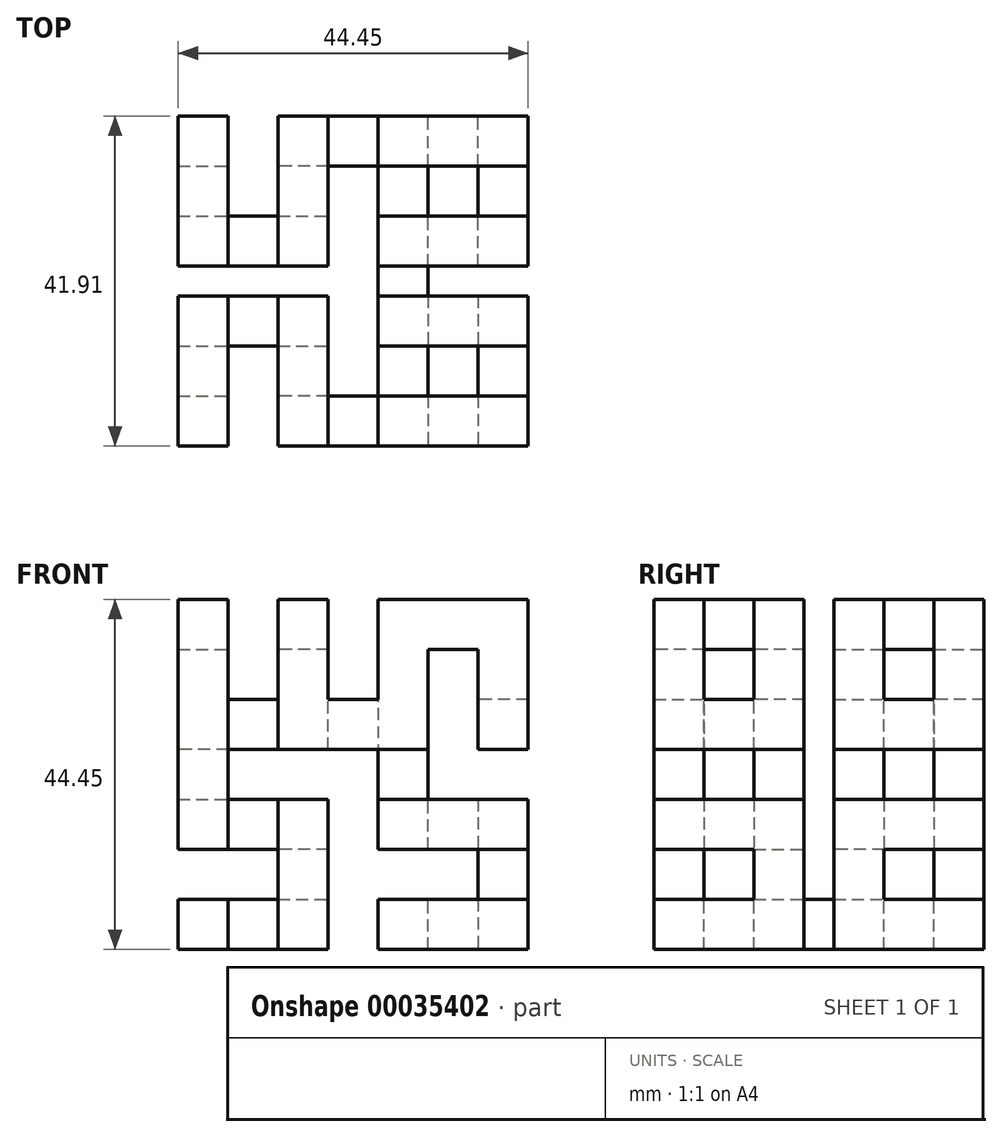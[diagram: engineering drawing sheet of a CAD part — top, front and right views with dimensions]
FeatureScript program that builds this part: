
annotation { "Feature Type Name" : "Feature", "Feature Type Description" : "" }
export const myFeature = defineFeature(function(context is Context, id is Id, definition is map)
    precondition{}
    {
        {
            var Q0;
            Q0=qCreatedBy(makeId("Front.planeOp"),FACE);
            var sketch = newSketch(context, id + "F0", { "sketchPlane" : qUnion([Q0])});
            skLineSegment(sketch, "E0.bottom", {"start": v(0, 0) * mm, "end": v(6.35, 0) * mm});
            skLineSegment(sketch, "E0.top", {"start": v(0, 6.35) * mm, "end": v(6.35, 6.35) * mm});
            skLineSegment(sketch, "E0.left", {"start": v(0, 0) * mm, "end": v(0, 6.35) * mm});
            skLineSegment(sketch, "E0.right", {"start": v(6.35, 0) * mm, "end": v(6.35, 6.35) * mm});
            skSolve(sketch);
        }
        {
            var Q0;
            Q0=makeQuery(id+"F0.imprint","IMPRINT",FACE,{"disambiguationData":[TD([[makeQuery(id+"F0.imprint","IMPRINT",EDGE,{"derivedFrom":sQuery(id+"F0.wireOp",EDGE,"E0.bottom")}),1.0]])]});
            extrude(context, id + "F1", {"entities" : qUnion([Q0]), "depth" : 19.05 * mm});
        }
        {
            var Q0;
            Q0=makeQuery(id+"F1.opExtrude","SWEPT_FACE",FACE,{"disambiguationData":[OSD([sQuery(id+"F0.wireOp",EDGE,"E0.left")])]});
            var sketch = newSketch(context, id + "F2", { "sketchPlane" : qUnion([Q0])});
            skLineSegment(sketch, "E1.bottom", {"start": v(19.05, 6.35) * mm, "end": v(12.7, 6.35) * mm});
            skLineSegment(sketch, "E1.top", {"start": v(19.05, 0) * mm, "end": v(12.7, 0) * mm});
            skLineSegment(sketch, "E1.left", {"start": v(19.05, 6.35) * mm, "end": v(19.05, 0) * mm});
            skLineSegment(sketch, "E1.right", {"start": v(12.7, 6.35) * mm, "end": v(12.7, 0) * mm});
            skSolve(sketch);
        }
        {
            var Q0;
            Q0=makeQuery(id+"F2.imprint","IMPRINT",FACE,{"disambiguationData":[TD([[makeQuery(id+"F2.imprint","IMPRINT",EDGE,{"derivedFrom":sQuery(id+"F2.wireOp",EDGE,"E1.bottom")}),1.0]])]});
            extrude(context, id + "F3", {"entities" : qUnion([Q0]), "operationType" : NewBodyOperationType.ADD, "oppositeDirection" : true, "depth" : 19.05 * mm});
        }
        {
            var Q0;
            Q0=makeQuery(id+"F3.boolean.opBoolean","MERGE",FACE,{"derivedFrom":[makeQuery(id+"F1.opExtrude","CAP_FACE",FACE,{"disambiguationData":[OSD([sQuery(id+"F0.wireOp",EDGE,"E0.bottom"),sQuery(id+"F0.wireOp",EDGE,"E0.top"),sQuery(id+"F0.wireOp",EDGE,"E0.left"),sQuery(id+"F0.wireOp",EDGE,"E0.right")])],"isStart":false}),makeQuery(id+"F3.opExtrude","SWEPT_FACE",FACE,{"disambiguationData":[OSD([sQuery(id+"F2.wireOp",EDGE,"E1.left")])]})]});
            var sketch = newSketch(context, id + "F4", { "sketchPlane" : qUnion([Q0])});
            skLineSegment(sketch, "E2.bottom", {"start": v(19.05, 6.35) * mm, "end": v(12.7, 6.35) * mm});
            skLineSegment(sketch, "E2.top", {"start": v(19.05, 0) * mm, "end": v(12.7, 0) * mm});
            skLineSegment(sketch, "E2.left", {"start": v(19.05, 6.35) * mm, "end": v(19.05, 0) * mm});
            skLineSegment(sketch, "E2.right", {"start": v(12.7, 6.35) * mm, "end": v(12.7, 0) * mm});
            skSolve(sketch);
        }
        {
            var Q0;
            Q0=makeQuery(id+"F4.imprint","IMPRINT",FACE,{"disambiguationData":[TD([[makeQuery(id+"F4.imprint","IMPRINT",EDGE,{"derivedFrom":sQuery(id+"F4.wireOp",EDGE,"E2.bottom")}),-1.0]])]});
            extrude(context, id + "F5", {"entities" : qUnion([Q0]), "operationType" : NewBodyOperationType.ADD, "oppositeDirection" : true, "depth" : 19.05 * mm});
        }
        {
            var Q0;
            Q0=makeQuery(id+"F5.boolean.opBoolean","MERGE",FACE,{"derivedFrom":[makeQuery(id+"F3.boolean.opBoolean","MERGE",FACE,{"derivedFrom":[makeQuery(id+"F1.opExtrude","SWEPT_FACE",FACE,{"disambiguationData":[OSD([sQuery(id+"F0.wireOp",EDGE,"E0.bottom")])]}),makeQuery(id+"F3.opExtrude","SWEPT_FACE",FACE,{"disambiguationData":[OSD([sQuery(id+"F2.wireOp",EDGE,"E1.top")])]})]}),makeQuery(id+"F5.opExtrude","SWEPT_FACE",FACE,{"disambiguationData":[OSD([sQuery(id+"F4.wireOp",EDGE,"E2.top")])]})]});
            var sketch = newSketch(context, id + "F6", { "sketchPlane" : qUnion([Q0])});
            skLineSegment(sketch, "E3.bottom", {"start": v(19.05, 0) * mm, "end": v(12.7, 0) * mm});
            skLineSegment(sketch, "E3.top", {"start": v(19.05, 6.35) * mm, "end": v(12.7, 6.35) * mm});
            skLineSegment(sketch, "E3.left", {"start": v(19.05, 0) * mm, "end": v(19.05, 6.35) * mm});
            skLineSegment(sketch, "E3.right", {"start": v(12.7, 0) * mm, "end": v(12.7, 6.35) * mm});
            skSolve(sketch);
        }
        {
            var Q0;
            Q0=makeQuery(id+"F6.imprint","IMPRINT",FACE,{"disambiguationData":[TD([[makeQuery(id+"F6.imprint","IMPRINT",EDGE,{"derivedFrom":sQuery(id+"F6.wireOp",EDGE,"E3.bottom")}),1.0]])]});
            extrude(context, id + "F7", {"entities" : qUnion([Q0]), "operationType" : NewBodyOperationType.ADD, "oppositeDirection" : true, "depth" : 19.05 * mm});
        }
        {
            var Q0;
            Q0=makeQuery(id+"F7.boolean.opBoolean","MERGE",FACE,{"derivedFrom":[makeQuery(id+"F5.opExtrude","CAP_FACE",FACE,{"disambiguationData":[OSD([sQuery(id+"F4.wireOp",EDGE,"E2.bottom"),sQuery(id+"F4.wireOp",EDGE,"E2.top"),sQuery(id+"F4.wireOp",EDGE,"E2.left"),sQuery(id+"F4.wireOp",EDGE,"E2.right")])],"isStart":false}),makeQuery(id+"F7.opExtrude","SWEPT_FACE",FACE,{"disambiguationData":[OSD([sQuery(id+"F6.wireOp",EDGE,"E3.bottom")])]})]});
            var sketch = newSketch(context, id + "F8", { "sketchPlane" : qUnion([Q0])});
            skLineSegment(sketch, "E4.bottom", {"start": v(-12.7, 19.05) * mm, "end": v(-19.05, 19.05) * mm});
            skLineSegment(sketch, "E4.top", {"start": v(-12.7, 12.7) * mm, "end": v(-19.05, 12.7) * mm});
            skLineSegment(sketch, "E4.left", {"start": v(-12.7, 19.05) * mm, "end": v(-12.7, 12.7) * mm});
            skLineSegment(sketch, "E4.right", {"start": v(-19.05, 19.05) * mm, "end": v(-19.05, 12.7) * mm});
            skSolve(sketch);
        }
        {
            var Q0;
            Q0=makeQuery(id+"F8.imprint","IMPRINT",FACE,{"disambiguationData":[TD([[makeQuery(id+"F8.imprint","IMPRINT",EDGE,{"derivedFrom":sQuery(id+"F8.wireOp",EDGE,"E4.bottom")}),1.0]])]});
            extrude(context, id + "F9", {"entities" : qUnion([Q0]), "operationType" : NewBodyOperationType.ADD, "oppositeDirection" : true, "depth" : 19.05 * mm});
        }
        {
            var Q0;
            Q0=makeQuery(id+"F9.boolean.opBoolean","MERGE",FACE,{"derivedFrom":[makeQuery(id+"F7.boolean.opBoolean","MERGE",FACE,{"derivedFrom":[makeQuery(id+"F5.boolean.opBoolean","MERGE",FACE,{"derivedFrom":[makeQuery(id+"F3.opExtrude","CAP_FACE",FACE,{"disambiguationData":[OSD([sQuery(id+"F2.wireOp",EDGE,"E1.bottom"),sQuery(id+"F2.wireOp",EDGE,"E1.top"),sQuery(id+"F2.wireOp",EDGE,"E1.left"),sQuery(id+"F2.wireOp",EDGE,"E1.right")])],"isStart":false}),makeQuery(id+"F5.opExtrude","SWEPT_FACE",FACE,{"disambiguationData":[OSD([sQuery(id+"F4.wireOp",EDGE,"E2.left")])]})]}),makeQuery(id+"F7.opExtrude","SWEPT_FACE",FACE,{"disambiguationData":[OSD([sQuery(id+"F6.wireOp",EDGE,"E3.left")])]})]}),makeQuery(id+"F9.opExtrude","SWEPT_FACE",FACE,{"disambiguationData":[OSD([sQuery(id+"F8.wireOp",EDGE,"E4.right")])]})]});
            var sketch = newSketch(context, id + "F10", { "sketchPlane" : qUnion([Q0])});
            skLineSegment(sketch, "E5.bottom", {"start": v(-19.05, 19.05) * mm, "end": v(-12.7, 19.05) * mm});
            skLineSegment(sketch, "E5.top", {"start": v(-19.05, 12.7) * mm, "end": v(-12.7, 12.7) * mm});
            skLineSegment(sketch, "E5.left", {"start": v(-19.05, 19.05) * mm, "end": v(-19.05, 12.7) * mm});
            skLineSegment(sketch, "E5.right", {"start": v(-12.7, 19.05) * mm, "end": v(-12.7, 12.7) * mm});
            skSolve(sketch);
        }
        {
            var Q0;
            Q0=makeQuery(id+"F10.imprint","IMPRINT",FACE,{"disambiguationData":[TD([[makeQuery(id+"F10.imprint","IMPRINT",EDGE,{"derivedFrom":sQuery(id+"F10.wireOp",EDGE,"E5.bottom")}),-1.0]])]});
            extrude(context, id + "F11", {"entities" : qUnion([Q0]), "operationType" : NewBodyOperationType.ADD, "oppositeDirection" : true, "depth" : 19.05 * mm});
        }
        {
            var Q0;
            Q0=makeQuery(id+"F11.boolean.opBoolean","MERGE",FACE,{"derivedFrom":[makeQuery(id+"F9.opExtrude","CAP_FACE",FACE,{"disambiguationData":[OSD([sQuery(id+"F8.wireOp",EDGE,"E4.bottom"),sQuery(id+"F8.wireOp",EDGE,"E4.top"),sQuery(id+"F8.wireOp",EDGE,"E4.left"),sQuery(id+"F8.wireOp",EDGE,"E4.right")])],"isStart":false}),makeQuery(id+"F11.opExtrude","SWEPT_FACE",FACE,{"disambiguationData":[OSD([sQuery(id+"F10.wireOp",EDGE,"E5.left")])]})]});
            var sketch = newSketch(context, id + "F12", { "sketchPlane" : qUnion([Q0])});
            skLineSegment(sketch, "E6.bottom", {"start": v(0, 19.05) * mm, "end": v(6.35, 19.05) * mm});
            skLineSegment(sketch, "E6.top", {"start": v(0, 12.7) * mm, "end": v(6.35, 12.7) * mm});
            skLineSegment(sketch, "E6.left", {"start": v(0, 19.05) * mm, "end": v(0, 12.7) * mm});
            skLineSegment(sketch, "E6.right", {"start": v(6.35, 19.05) * mm, "end": v(6.35, 12.7) * mm});
            skSolve(sketch);
        }
        {
            var Q0;
            Q0=makeQuery(id+"F12.imprint","IMPRINT",FACE,{"disambiguationData":[TD([[makeQuery(id+"F12.imprint","IMPRINT",EDGE,{"derivedFrom":sQuery(id+"F12.wireOp",EDGE,"E6.bottom")}),-1.0]])]});
            extrude(context, id + "F13", {"entities" : qUnion([Q0]), "operationType" : NewBodyOperationType.ADD, "oppositeDirection" : true, "depth" : 19.05 * mm});
        }
        {
            var Q0;
            Q0=makeQuery(id+"F13.boolean.opBoolean","MERGE",FACE,{"derivedFrom":[makeQuery(id+"F11.boolean.opBoolean","MERGE",FACE,{"derivedFrom":[makeQuery(id+"F9.opExtrude","SWEPT_FACE",FACE,{"disambiguationData":[OSD([sQuery(id+"F8.wireOp",EDGE,"E4.top")])]}),makeQuery(id+"F11.opExtrude","SWEPT_FACE",FACE,{"disambiguationData":[OSD([sQuery(id+"F10.wireOp",EDGE,"E5.top")])]})]}),makeQuery(id+"F13.opExtrude","SWEPT_FACE",FACE,{"disambiguationData":[OSD([sQuery(id+"F12.wireOp",EDGE,"E6.top")])]})]});
            var sketch = newSketch(context, id + "F14", { "sketchPlane" : qUnion([Q0])});
            skLineSegment(sketch, "E7.bottom", {"start": v(0, 0) * mm, "end": v(6.35, 0) * mm});
            skLineSegment(sketch, "E7.top", {"start": v(0, 6.35) * mm, "end": v(6.35, 6.35) * mm});
            skLineSegment(sketch, "E7.left", {"start": v(0, 0) * mm, "end": v(0, 6.35) * mm});
            skLineSegment(sketch, "E7.right", {"start": v(6.35, 0) * mm, "end": v(6.35, 6.35) * mm});
            skSolve(sketch);
        }
        {
            var Q0;
            Q0=makeQuery(id+"F14.imprint","IMPRINT",FACE,{"disambiguationData":[TD([[makeQuery(id+"F14.imprint","IMPRINT",EDGE,{"derivedFrom":sQuery(id+"F14.wireOp",EDGE,"E7.bottom")}),1.0]])]});
            extrude(context, id + "F15", {"entities" : qUnion([Q0]), "operationType" : NewBodyOperationType.ADD, "oppositeDirection" : true, "depth" : 31.75 * mm});
        }
        {
            var Q0;
            Q0=makeQuery(id+"F15.boolean.opBoolean","MERGE",FACE,{"derivedFrom":[makeQuery(id+"F13.opExtrude","CAP_FACE",FACE,{"disambiguationData":[OSD([sQuery(id+"F12.wireOp",EDGE,"E6.bottom"),sQuery(id+"F12.wireOp",EDGE,"E6.top"),sQuery(id+"F12.wireOp",EDGE,"E6.left"),sQuery(id+"F12.wireOp",EDGE,"E6.right")])],"isStart":false}),makeQuery(id+"F15.opExtrude","SWEPT_FACE",FACE,{"disambiguationData":[OSD([sQuery(id+"F14.wireOp",EDGE,"E7.bottom")])]})]});
            var sketch = newSketch(context, id + "F16", { "sketchPlane" : qUnion([Q0])});
            skLineSegment(sketch, "E8.bottom", {"start": v(-6.35, 44.45) * mm, "end": v(0, 44.45) * mm});
            skLineSegment(sketch, "E8.top", {"start": v(-6.35, 38.1) * mm, "end": v(0, 38.1) * mm});
            skLineSegment(sketch, "E8.left", {"start": v(-6.35, 44.45) * mm, "end": v(-6.35, 38.1) * mm});
            skLineSegment(sketch, "E8.right", {"start": v(0, 44.45) * mm, "end": v(0, 38.1) * mm});
            skSolve(sketch);
        }
        {
            var Q0;
            Q0=makeQuery(id+"F16.imprint","IMPRINT",FACE,{"disambiguationData":[TD([[makeQuery(id+"F16.imprint","IMPRINT",EDGE,{"derivedFrom":sQuery(id+"F16.wireOp",EDGE,"E8.bottom")}),1.0]])]});
            extrude(context, id + "F17", {"entities" : qUnion([Q0]), "operationType" : NewBodyOperationType.ADD, "oppositeDirection" : true, "depth" : 19.05 * mm});
        }
        {
            var Q0;
            Q0=makeQuery(id+"F17.boolean.opBoolean","MERGE",FACE,{"derivedFrom":[makeQuery(id+"F15.opExtrude","CAP_FACE",FACE,{"disambiguationData":[OSD([sQuery(id+"F14.wireOp",EDGE,"E7.bottom"),sQuery(id+"F14.wireOp",EDGE,"E7.top"),sQuery(id+"F14.wireOp",EDGE,"E7.left"),sQuery(id+"F14.wireOp",EDGE,"E7.right")])],"isStart":false}),makeQuery(id+"F17.opExtrude","SWEPT_FACE",FACE,{"disambiguationData":[OSD([sQuery(id+"F16.wireOp",EDGE,"E8.bottom")])]})]});
            var sketch = newSketch(context, id + "F18", { "sketchPlane" : qUnion([Q0])});
            skLineSegment(sketch, "E9.bottom", {"start": v(6.35, -19.05) * mm, "end": v(0, -19.05) * mm});
            skLineSegment(sketch, "E9.top", {"start": v(6.35, -12.7) * mm, "end": v(0, -12.7) * mm});
            skLineSegment(sketch, "E9.left", {"start": v(6.35, -19.05) * mm, "end": v(6.35, -12.7) * mm});
            skLineSegment(sketch, "E9.right", {"start": v(0, -19.05) * mm, "end": v(0, -12.7) * mm});
            skSolve(sketch);
        }
        {
            var Q0;
            Q0=makeQuery(id+"F18.imprint","IMPRINT",FACE,{"disambiguationData":[TD([[makeQuery(id+"F18.imprint","IMPRINT",EDGE,{"derivedFrom":sQuery(id+"F18.wireOp",EDGE,"E9.bottom")}),1.0]])]});
            extrude(context, id + "F19", {"entities" : qUnion([Q0]), "operationType" : NewBodyOperationType.ADD, "oppositeDirection" : true, "depth" : 19.05 * mm});
        }
        {
            var Q0;
            Q0=makeQuery(id+"F19.boolean.opBoolean","MERGE",FACE,{"derivedFrom":[makeQuery(id+"F17.boolean.opBoolean","MERGE",FACE,{"derivedFrom":[makeQuery(id+"F15.boolean.opBoolean","MERGE",FACE,{"derivedFrom":[makeQuery(id+"F13.boolean.opBoolean","MERGE",FACE,{"derivedFrom":[makeQuery(id+"F11.opExtrude","CAP_FACE",FACE,{"disambiguationData":[OSD([sQuery(id+"F10.wireOp",EDGE,"E5.bottom"),sQuery(id+"F10.wireOp",EDGE,"E5.top"),sQuery(id+"F10.wireOp",EDGE,"E5.left"),sQuery(id+"F10.wireOp",EDGE,"E5.right")])],"isStart":false}),makeQuery(id+"F13.opExtrude","SWEPT_FACE",FACE,{"disambiguationData":[OSD([sQuery(id+"F12.wireOp",EDGE,"E6.left")])]})]}),makeQuery(id+"F15.opExtrude","SWEPT_FACE",FACE,{"disambiguationData":[OSD([sQuery(id+"F14.wireOp",EDGE,"E7.left")])]})]}),makeQuery(id+"F17.opExtrude","SWEPT_FACE",FACE,{"disambiguationData":[OSD([sQuery(id+"F16.wireOp",EDGE,"E8.right")])]})]}),makeQuery(id+"F19.opExtrude","SWEPT_FACE",FACE,{"disambiguationData":[OSD([sQuery(id+"F18.wireOp",EDGE,"E9.right")])]})]});
            var sketch = newSketch(context, id + "F20", { "sketchPlane" : qUnion([Q0])});
            skLineSegment(sketch, "E10.bottom", {"start": v(19.05, 25.4) * mm, "end": v(12.7, 25.4) * mm});
            skLineSegment(sketch, "E10.top", {"start": v(19.05, 31.75) * mm, "end": v(12.7, 31.75) * mm});
            skLineSegment(sketch, "E10.left", {"start": v(19.05, 25.4) * mm, "end": v(19.05, 31.75) * mm});
            skLineSegment(sketch, "E10.right", {"start": v(12.7, 25.4) * mm, "end": v(12.7, 31.75) * mm});
            skSolve(sketch);
        }
        {
            var Q0;
            Q0=makeQuery(id+"F20.imprint","IMPRINT",FACE,{"disambiguationData":[TD([[makeQuery(id+"F20.imprint","IMPRINT",EDGE,{"derivedFrom":sQuery(id+"F20.wireOp",EDGE,"E10.bottom")}),-1.0]])]});
            extrude(context, id + "F21", {"entities" : qUnion([Q0]), "operationType" : NewBodyOperationType.ADD, "oppositeDirection" : true, "depth" : 19.05 * mm});
        }
        {
            var Q0;
            Q0=makeQuery(id+"F21.boolean.opBoolean","MERGE",FACE,{"derivedFrom":[makeQuery(id+"F19.opExtrude","CAP_FACE",FACE,{"disambiguationData":[OSD([sQuery(id+"F18.wireOp",EDGE,"E9.bottom"),sQuery(id+"F18.wireOp",EDGE,"E9.top"),sQuery(id+"F18.wireOp",EDGE,"E9.left"),sQuery(id+"F18.wireOp",EDGE,"E9.right")])],"isStart":false}),makeQuery(id+"F21.opExtrude","SWEPT_FACE",FACE,{"disambiguationData":[OSD([sQuery(id+"F20.wireOp",EDGE,"E10.bottom")])]})]});
            var sketch = newSketch(context, id + "F22", { "sketchPlane" : qUnion([Q0])});
            skLineSegment(sketch, "E11.bottom", {"start": v(19.05, 19.05) * mm, "end": v(12.7, 19.05) * mm});
            skLineSegment(sketch, "E11.top", {"start": v(19.05, 12.7) * mm, "end": v(12.7, 12.7) * mm});
            skLineSegment(sketch, "E11.left", {"start": v(19.05, 19.05) * mm, "end": v(19.05, 12.7) * mm});
            skLineSegment(sketch, "E11.right", {"start": v(12.7, 19.05) * mm, "end": v(12.7, 12.7) * mm});
            skSolve(sketch);
        }
        {
            var Q0;
            Q0=makeQuery(id+"F22.imprint","IMPRINT",FACE,{"disambiguationData":[TD([[makeQuery(id+"F22.imprint","IMPRINT",EDGE,{"derivedFrom":sQuery(id+"F22.wireOp",EDGE,"E11.bottom")}),-1.0]])]});
            extrude(context, id + "F23", {"entities" : qUnion([Q0]), "operationType" : NewBodyOperationType.ADD, "oppositeDirection" : true, "depth" : 19.05 * mm});
        }
        {
            var Q0;
            Q0=makeQuery(id+"F23.boolean.opBoolean","MERGE",FACE,{"derivedFrom":[makeQuery(id+"F21.boolean.opBoolean","MERGE",FACE,{"derivedFrom":[makeQuery(id+"F19.boolean.opBoolean","MERGE",FACE,{"derivedFrom":[makeQuery(id+"F17.opExtrude","CAP_FACE",FACE,{"disambiguationData":[OSD([sQuery(id+"F16.wireOp",EDGE,"E8.bottom"),sQuery(id+"F16.wireOp",EDGE,"E8.top"),sQuery(id+"F16.wireOp",EDGE,"E8.left"),sQuery(id+"F16.wireOp",EDGE,"E8.right")])],"isStart":false}),makeQuery(id+"F19.opExtrude","SWEPT_FACE",FACE,{"disambiguationData":[OSD([sQuery(id+"F18.wireOp",EDGE,"E9.bottom")])]})]}),makeQuery(id+"F21.opExtrude","SWEPT_FACE",FACE,{"disambiguationData":[OSD([sQuery(id+"F20.wireOp",EDGE,"E10.left")])]})]}),makeQuery(id+"F23.opExtrude","SWEPT_FACE",FACE,{"disambiguationData":[OSD([sQuery(id+"F22.wireOp",EDGE,"E11.bottom")])]})]});
            var sketch = newSketch(context, id + "F24", { "sketchPlane" : qUnion([Q0])});
            skLineSegment(sketch, "E12.bottom", {"start": v(19.05, 44.45) * mm, "end": v(12.7, 44.45) * mm});
            skLineSegment(sketch, "E12.top", {"start": v(19.05, 38.1) * mm, "end": v(12.7, 38.1) * mm});
            skLineSegment(sketch, "E12.left", {"start": v(19.05, 44.45) * mm, "end": v(19.05, 38.1) * mm});
            skLineSegment(sketch, "E12.right", {"start": v(12.7, 44.45) * mm, "end": v(12.7, 38.1) * mm});
            skSolve(sketch);
        }
        {
            var Q0;
            Q0=makeQuery(id+"F24.imprint","IMPRINT",FACE,{"disambiguationData":[TD([[makeQuery(id+"F24.imprint","IMPRINT",EDGE,{"derivedFrom":sQuery(id+"F24.wireOp",EDGE,"E12.bottom")}),-1.0]])]});
            extrude(context, id + "F25", {"entities" : qUnion([Q0]), "operationType" : NewBodyOperationType.ADD, "oppositeDirection" : true, "depth" : 19.05 * mm});
        }
        {
            var Q0;
            Q0=makeQuery(id+"F25.boolean.opBoolean","MERGE",FACE,{"derivedFrom":[makeQuery(id+"F23.opExtrude","CAP_FACE",FACE,{"disambiguationData":[OSD([sQuery(id+"F22.wireOp",EDGE,"E11.bottom"),sQuery(id+"F22.wireOp",EDGE,"E11.top"),sQuery(id+"F22.wireOp",EDGE,"E11.left"),sQuery(id+"F22.wireOp",EDGE,"E11.right")])],"isStart":false}),makeQuery(id+"F25.opExtrude","SWEPT_FACE",FACE,{"disambiguationData":[OSD([sQuery(id+"F24.wireOp",EDGE,"E12.bottom")])]})]});
            var sketch = newSketch(context, id + "F26", { "sketchPlane" : qUnion([Q0])});
            skLineSegment(sketch, "E13.bottom", {"start": v(19.05, 0) * mm, "end": v(12.7, 0) * mm});
            skLineSegment(sketch, "E13.top", {"start": v(19.05, -6.35) * mm, "end": v(12.7, -6.35) * mm});
            skLineSegment(sketch, "E13.left", {"start": v(19.05, 0) * mm, "end": v(19.05, -6.35) * mm});
            skLineSegment(sketch, "E13.right", {"start": v(12.7, 0) * mm, "end": v(12.7, -6.35) * mm});
            skSolve(sketch);
        }
        {
            var Q0;
            Q0=makeQuery(id+"F26.imprint","IMPRINT",FACE,{"disambiguationData":[TD([[makeQuery(id+"F26.imprint","IMPRINT",EDGE,{"derivedFrom":sQuery(id+"F26.wireOp",EDGE,"E13.bottom")}),-1.0]])]});
            extrude(context, id + "F27", {"entities" : qUnion([Q0]), "operationType" : NewBodyOperationType.ADD, "oppositeDirection" : true, "depth" : 19.05 * mm});
        }
        {
            var Q0;
            Q0=makeQuery(id+"F27.boolean.opBoolean","MERGE",FACE,{"derivedFrom":[makeQuery(id+"F25.boolean.opBoolean","MERGE",FACE,{"derivedFrom":[makeQuery(id+"F23.opExtrude","SWEPT_FACE",FACE,{"disambiguationData":[OSD([sQuery(id+"F22.wireOp",EDGE,"E11.right")])]}),makeQuery(id+"F25.opExtrude","SWEPT_FACE",FACE,{"disambiguationData":[OSD([sQuery(id+"F24.wireOp",EDGE,"E12.right")])]})]}),makeQuery(id+"F27.opExtrude","SWEPT_FACE",FACE,{"disambiguationData":[OSD([sQuery(id+"F26.wireOp",EDGE,"E13.right")])]})]});
            var sketch = newSketch(context, id + "F28", { "sketchPlane" : qUnion([Q0])});
            skLineSegment(sketch, "E14.bottom", {"start": v(0, 25.4) * mm, "end": v(6.35, 25.4) * mm});
            skLineSegment(sketch, "E14.top", {"start": v(0, 31.75) * mm, "end": v(6.35, 31.75) * mm});
            skLineSegment(sketch, "E14.left", {"start": v(0, 25.4) * mm, "end": v(0, 31.75) * mm});
            skLineSegment(sketch, "E14.right", {"start": v(6.35, 25.4) * mm, "end": v(6.35, 31.75) * mm});
            skSolve(sketch);
        }
        {
            var Q0;
            Q0=makeQuery(id+"F28.imprint","IMPRINT",FACE,{"disambiguationData":[TD([[makeQuery(id+"F28.imprint","IMPRINT",EDGE,{"derivedFrom":sQuery(id+"F28.wireOp",EDGE,"E14.bottom")}),-1.0]])]});
            extrude(context, id + "F29", {"entities" : qUnion([Q0]), "operationType" : NewBodyOperationType.ADD, "oppositeDirection" : true, "depth" : 19.05 * mm});
        }
        {
            var Q0;
            Q0=makeQuery(id+"F29.boolean.opBoolean","MERGE",FACE,{"derivedFrom":[makeQuery(id+"F27.opExtrude","CAP_FACE",FACE,{"disambiguationData":[OSD([sQuery(id+"F26.wireOp",EDGE,"E13.bottom"),sQuery(id+"F26.wireOp",EDGE,"E13.top"),sQuery(id+"F26.wireOp",EDGE,"E13.left"),sQuery(id+"F26.wireOp",EDGE,"E13.right")])],"isStart":false}),makeQuery(id+"F29.opExtrude","SWEPT_FACE",FACE,{"disambiguationData":[OSD([sQuery(id+"F28.wireOp",EDGE,"E14.bottom")])]})]});
            var sketch = newSketch(context, id + "F30", { "sketchPlane" : qUnion([Q0])});
            skLineSegment(sketch, "E15.bottom", {"start": v(31.75, 0) * mm, "end": v(25.4, 0) * mm});
            skLineSegment(sketch, "E15.top", {"start": v(31.75, 6.35) * mm, "end": v(25.4, 6.35) * mm});
            skLineSegment(sketch, "E15.left", {"start": v(31.75, 0) * mm, "end": v(31.75, 6.35) * mm});
            skLineSegment(sketch, "E15.right", {"start": v(25.4, 0) * mm, "end": v(25.4, 6.35) * mm});
            skSolve(sketch);
        }
        {
            var Q0;
            Q0=makeQuery(id+"F30.imprint","IMPRINT",FACE,{"disambiguationData":[TD([[makeQuery(id+"F30.imprint","IMPRINT",EDGE,{"derivedFrom":sQuery(id+"F30.wireOp",EDGE,"E15.bottom")}),1.0]])]});
            extrude(context, id + "F31", {"entities" : qUnion([Q0]), "operationType" : NewBodyOperationType.ADD, "oppositeDirection" : true, "depth" : 19.05 * mm});
        }
        {
            var Q0;
            Q0=makeQuery(id+"F31.opExtrude","SWEPT_FACE",FACE,{"disambiguationData":[OSD([sQuery(id+"F30.wireOp",EDGE,"E15.right")])]});
            var sketch = newSketch(context, id + "F32", { "sketchPlane" : qUnion([Q0])});
            skLineSegment(sketch, "E16.bottom", {"start": v(6.35, 44.45) * mm, "end": v(0, 44.45) * mm});
            skLineSegment(sketch, "E16.top", {"start": v(6.35, 38.1) * mm, "end": v(0, 38.1) * mm});
            skLineSegment(sketch, "E16.left", {"start": v(6.35, 44.45) * mm, "end": v(6.35, 38.1) * mm});
            skLineSegment(sketch, "E16.right", {"start": v(0, 44.45) * mm, "end": v(0, 38.1) * mm});
            skSolve(sketch);
        }
        {
            var Q0;
            Q0=makeQuery(id+"F32.imprint","IMPRINT",FACE,{"disambiguationData":[TD([[makeQuery(id+"F32.imprint","IMPRINT",EDGE,{"derivedFrom":sQuery(id+"F32.wireOp",EDGE,"E16.bottom")}),-1.0]])]});
            extrude(context, id + "F33", {"entities" : qUnion([Q0]), "operationType" : NewBodyOperationType.ADD, "oppositeDirection" : true, "depth" : 19.05 * mm});
        }
        {
            var Q0;
            Q0=makeQuery(id+"F33.boolean.opBoolean","MERGE",FACE,{"derivedFrom":[makeQuery(id+"F31.opExtrude","CAP_FACE",FACE,{"disambiguationData":[OSD([sQuery(id+"F30.wireOp",EDGE,"E15.bottom"),sQuery(id+"F30.wireOp",EDGE,"E15.top"),sQuery(id+"F30.wireOp",EDGE,"E15.left"),sQuery(id+"F30.wireOp",EDGE,"E15.right")])],"isStart":false}),makeQuery(id+"F33.opExtrude","SWEPT_FACE",FACE,{"disambiguationData":[OSD([sQuery(id+"F32.wireOp",EDGE,"E16.bottom")])]})]});
            var sketch = newSketch(context, id + "F34", { "sketchPlane" : qUnion([Q0])});
            skLineSegment(sketch, "E17.bottom", {"start": v(44.45, -6.35) * mm, "end": v(38.1, -6.35) * mm});
            skLineSegment(sketch, "E17.top", {"start": v(44.45, 0) * mm, "end": v(38.1, 0) * mm});
            skLineSegment(sketch, "E17.left", {"start": v(44.45, -6.35) * mm, "end": v(44.45, 0) * mm});
            skLineSegment(sketch, "E17.right", {"start": v(38.1, -6.35) * mm, "end": v(38.1, 0) * mm});
            skSolve(sketch);
        }
        {
            var Q0;
            Q0=makeQuery(id+"F34.imprint","IMPRINT",FACE,{"disambiguationData":[TD([[makeQuery(id+"F34.imprint","IMPRINT",EDGE,{"derivedFrom":sQuery(id+"F34.wireOp",EDGE,"E17.bottom")}),-1.0]])]});
            extrude(context, id + "F35", {"entities" : qUnion([Q0]), "operationType" : NewBodyOperationType.ADD, "oppositeDirection" : true, "depth" : 19.05 * mm});
        }
        {
            var Q0;
            Q0=makeQuery(id+"F35.boolean.opBoolean","MERGE",FACE,{"derivedFrom":[makeQuery(id+"F33.boolean.opBoolean","MERGE",FACE,{"derivedFrom":[makeQuery(id+"F31.boolean.opBoolean","MERGE",FACE,{"derivedFrom":[makeQuery(id+"F29.boolean.opBoolean","MERGE",FACE,{"derivedFrom":[makeQuery(id+"F27.boolean.opBoolean","MERGE",FACE,{"derivedFrom":[makeQuery(id+"F25.opExtrude","CAP_FACE",FACE,{"disambiguationData":[OSD([sQuery(id+"F24.wireOp",EDGE,"E12.bottom"),sQuery(id+"F24.wireOp",EDGE,"E12.top"),sQuery(id+"F24.wireOp",EDGE,"E12.left"),sQuery(id+"F24.wireOp",EDGE,"E12.right")])],"isStart":false}),makeQuery(id+"F27.opExtrude","SWEPT_FACE",FACE,{"disambiguationData":[OSD([sQuery(id+"F26.wireOp",EDGE,"E13.bottom")])]})]}),makeQuery(id+"F29.opExtrude","SWEPT_FACE",FACE,{"disambiguationData":[OSD([sQuery(id+"F28.wireOp",EDGE,"E14.left")])]})]}),makeQuery(id+"F31.opExtrude","SWEPT_FACE",FACE,{"disambiguationData":[OSD([sQuery(id+"F30.wireOp",EDGE,"E15.bottom")])]})]}),makeQuery(id+"F33.opExtrude","SWEPT_FACE",FACE,{"disambiguationData":[OSD([sQuery(id+"F32.wireOp",EDGE,"E16.right")])]})]}),makeQuery(id+"F35.opExtrude","SWEPT_FACE",FACE,{"disambiguationData":[OSD([sQuery(id+"F34.wireOp",EDGE,"E17.top")])]})]});
            var sketch = newSketch(context, id + "F36", { "sketchPlane" : qUnion([Q0])});
            skLineSegment(sketch, "E18.bottom", {"start": v(-44.45, 25.4) * mm, "end": v(-38.1, 25.4) * mm});
            skLineSegment(sketch, "E18.top", {"start": v(-44.45, 31.75) * mm, "end": v(-38.1, 31.75) * mm});
            skLineSegment(sketch, "E18.left", {"start": v(-44.45, 25.4) * mm, "end": v(-44.45, 31.75) * mm});
            skLineSegment(sketch, "E18.right", {"start": v(-38.1, 25.4) * mm, "end": v(-38.1, 31.75) * mm});
            skSolve(sketch);
        }
        {
            var Q0;
            Q0=makeQuery(id+"F36.imprint","IMPRINT",FACE,{"disambiguationData":[TD([[makeQuery(id+"F36.imprint","IMPRINT",EDGE,{"derivedFrom":sQuery(id+"F36.wireOp",EDGE,"E18.bottom")}),-1.0]])]});
            extrude(context, id + "F37", {"entities" : qUnion([Q0]), "operationType" : NewBodyOperationType.ADD, "oppositeDirection" : true, "depth" : 19.05 * mm});
        }
        {
            var Q0;
            Q0=makeQuery(id+"F37.boolean.opBoolean","MERGE",FACE,{"derivedFrom":[makeQuery(id+"F35.opExtrude","CAP_FACE",FACE,{"disambiguationData":[OSD([sQuery(id+"F34.wireOp",EDGE,"E17.bottom"),sQuery(id+"F34.wireOp",EDGE,"E17.top"),sQuery(id+"F34.wireOp",EDGE,"E17.left"),sQuery(id+"F34.wireOp",EDGE,"E17.right")])],"isStart":false}),makeQuery(id+"F37.opExtrude","SWEPT_FACE",FACE,{"disambiguationData":[OSD([sQuery(id+"F36.wireOp",EDGE,"E18.bottom")])]})]});
            var sketch = newSketch(context, id + "F38", { "sketchPlane" : qUnion([Q0])});
            skLineSegment(sketch, "E19.bottom", {"start": v(38.1, 19.05) * mm, "end": v(44.45, 19.05) * mm});
            skLineSegment(sketch, "E19.top", {"start": v(38.1, 12.7) * mm, "end": v(44.45, 12.7) * mm});
            skLineSegment(sketch, "E19.left", {"start": v(38.1, 19.05) * mm, "end": v(38.1, 12.7) * mm});
            skLineSegment(sketch, "E19.right", {"start": v(44.45, 19.05) * mm, "end": v(44.45, 12.7) * mm});
            skSolve(sketch);
        }
        {
            var Q0;
            Q0=makeQuery(id+"F38.imprint","IMPRINT",FACE,{"disambiguationData":[TD([[makeQuery(id+"F38.imprint","IMPRINT",EDGE,{"derivedFrom":sQuery(id+"F38.wireOp",EDGE,"E19.bottom")}),-1.0]])]});
            extrude(context, id + "F39", {"entities" : qUnion([Q0]), "operationType" : NewBodyOperationType.ADD, "oppositeDirection" : true, "depth" : 19.05 * mm});
        }
        {
            var Q0;
            Q0=makeQuery(id+"F39.boolean.opBoolean","MERGE",FACE,{"derivedFrom":[makeQuery(id+"F37.boolean.opBoolean","MERGE",FACE,{"derivedFrom":[makeQuery(id+"F35.boolean.opBoolean","MERGE",FACE,{"derivedFrom":[makeQuery(id+"F33.opExtrude","CAP_FACE",FACE,{"disambiguationData":[OSD([sQuery(id+"F32.wireOp",EDGE,"E16.bottom"),sQuery(id+"F32.wireOp",EDGE,"E16.top"),sQuery(id+"F32.wireOp",EDGE,"E16.left"),sQuery(id+"F32.wireOp",EDGE,"E16.right")])],"isStart":false}),makeQuery(id+"F35.opExtrude","SWEPT_FACE",FACE,{"disambiguationData":[OSD([sQuery(id+"F34.wireOp",EDGE,"E17.left")])]})]}),makeQuery(id+"F37.opExtrude","SWEPT_FACE",FACE,{"disambiguationData":[OSD([sQuery(id+"F36.wireOp",EDGE,"E18.left")])]})]}),makeQuery(id+"F39.opExtrude","SWEPT_FACE",FACE,{"disambiguationData":[OSD([sQuery(id+"F38.wireOp",EDGE,"E19.right")])]})]});
            var sketch = newSketch(context, id + "F40", { "sketchPlane" : qUnion([Q0])});
            skLineSegment(sketch, "E20.bottom", {"start": v(-19.05, 44.45) * mm, "end": v(-12.7, 44.45) * mm});
            skLineSegment(sketch, "E20.top", {"start": v(-19.05, 38.1) * mm, "end": v(-12.7, 38.1) * mm});
            skLineSegment(sketch, "E20.left", {"start": v(-19.05, 44.45) * mm, "end": v(-19.05, 38.1) * mm});
            skLineSegment(sketch, "E20.right", {"start": v(-12.7, 44.45) * mm, "end": v(-12.7, 38.1) * mm});
            skSolve(sketch);
        }
        {
            var Q0;
            Q0=makeQuery(id+"F40.imprint","IMPRINT",FACE,{"disambiguationData":[TD([[makeQuery(id+"F40.imprint","IMPRINT",EDGE,{"derivedFrom":sQuery(id+"F40.wireOp",EDGE,"E20.bottom")}),1.0]])]});
            extrude(context, id + "F41", {"entities" : qUnion([Q0]), "operationType" : NewBodyOperationType.ADD, "oppositeDirection" : true, "depth" : 19.05 * mm});
        }
        {
            var Q0;
            Q0=makeQuery(id+"F41.boolean.opBoolean","MERGE",FACE,{"derivedFrom":[makeQuery(id+"F39.opExtrude","CAP_FACE",FACE,{"disambiguationData":[OSD([sQuery(id+"F38.wireOp",EDGE,"E19.bottom"),sQuery(id+"F38.wireOp",EDGE,"E19.top"),sQuery(id+"F38.wireOp",EDGE,"E19.left"),sQuery(id+"F38.wireOp",EDGE,"E19.right")])],"isStart":false}),makeQuery(id+"F41.opExtrude","SWEPT_FACE",FACE,{"disambiguationData":[OSD([sQuery(id+"F40.wireOp",EDGE,"E20.bottom")])]})]});
            var sketch = newSketch(context, id + "F42", { "sketchPlane" : qUnion([Q0])});
            skLineSegment(sketch, "E21.bottom", {"start": v(25.4, -12.7) * mm, "end": v(31.75, -12.7) * mm});
            skLineSegment(sketch, "E21.top", {"start": v(25.4, -19.05) * mm, "end": v(31.75, -19.05) * mm});
            skLineSegment(sketch, "E21.left", {"start": v(25.4, -12.7) * mm, "end": v(25.4, -19.05) * mm});
            skLineSegment(sketch, "E21.right", {"start": v(31.75, -12.7) * mm, "end": v(31.75, -19.05) * mm});
            skSolve(sketch);
        }
        {
            var Q0;
            Q0=makeQuery(id+"F42.imprint","IMPRINT",FACE,{"disambiguationData":[TD([[makeQuery(id+"F42.imprint","IMPRINT",EDGE,{"derivedFrom":sQuery(id+"F42.wireOp",EDGE,"E21.bottom")}),-1.0]])]});
            extrude(context, id + "F43", {"entities" : qUnion([Q0]), "operationType" : NewBodyOperationType.ADD, "oppositeDirection" : true, "depth" : 31.75 * mm});
        }
        {
            var Q0;
            Q0=makeQuery(id+"F43.boolean.opBoolean","MERGE",FACE,{"derivedFrom":[makeQuery(id+"F41.boolean.opBoolean","MERGE",FACE,{"derivedFrom":[makeQuery(id+"F39.boolean.opBoolean","MERGE",FACE,{"derivedFrom":[makeQuery(id+"F37.opExtrude","CAP_FACE",FACE,{"disambiguationData":[OSD([sQuery(id+"F36.wireOp",EDGE,"E18.bottom"),sQuery(id+"F36.wireOp",EDGE,"E18.top"),sQuery(id+"F36.wireOp",EDGE,"E18.left"),sQuery(id+"F36.wireOp",EDGE,"E18.right")])],"isStart":false}),makeQuery(id+"F39.opExtrude","SWEPT_FACE",FACE,{"disambiguationData":[OSD([sQuery(id+"F38.wireOp",EDGE,"E19.bottom")])]})]}),makeQuery(id+"F41.opExtrude","SWEPT_FACE",FACE,{"disambiguationData":[OSD([sQuery(id+"F40.wireOp",EDGE,"E20.left")])]})]}),makeQuery(id+"F43.opExtrude","SWEPT_FACE",FACE,{"disambiguationData":[OSD([sQuery(id+"F42.wireOp",EDGE,"E21.top")])]})]});
            var sketch = newSketch(context, id + "F44", { "sketchPlane" : qUnion([Q0])});
            skLineSegment(sketch, "E22.bottom", {"start": v(31.75, 12.7) * mm, "end": v(25.4, 12.7) * mm});
            skLineSegment(sketch, "E22.top", {"start": v(31.75, 19.05) * mm, "end": v(25.4, 19.05) * mm});
            skLineSegment(sketch, "E22.left", {"start": v(31.75, 12.7) * mm, "end": v(31.75, 19.05) * mm});
            skLineSegment(sketch, "E22.right", {"start": v(25.4, 12.7) * mm, "end": v(25.4, 19.05) * mm});
            skSolve(sketch);
        }
        {
            var Q0;
            Q0=makeQuery(id+"F44.imprint","IMPRINT",FACE,{"disambiguationData":[TD([[makeQuery(id+"F44.imprint","IMPRINT",EDGE,{"derivedFrom":sQuery(id+"F44.wireOp",EDGE,"E22.bottom")}),1.0]])]});
            extrude(context, id + "F45", {"entities" : qUnion([Q0]), "operationType" : NewBodyOperationType.ADD, "oppositeDirection" : true, "depth" : 19.05 * mm});
        }
        {
            var Q0;
            Q0=makeQuery(id+"F45.boolean.opBoolean","MERGE",FACE,{"derivedFrom":[makeQuery(id+"F43.boolean.opBoolean","MERGE",FACE,{"derivedFrom":[makeQuery(id+"F41.opExtrude","CAP_FACE",FACE,{"disambiguationData":[OSD([sQuery(id+"F40.wireOp",EDGE,"E20.bottom"),sQuery(id+"F40.wireOp",EDGE,"E20.top"),sQuery(id+"F40.wireOp",EDGE,"E20.left"),sQuery(id+"F40.wireOp",EDGE,"E20.right")])],"isStart":false}),makeQuery(id+"F43.opExtrude","SWEPT_FACE",FACE,{"disambiguationData":[OSD([sQuery(id+"F42.wireOp",EDGE,"E21.left")])]})]}),makeQuery(id+"F45.opExtrude","SWEPT_FACE",FACE,{"disambiguationData":[OSD([sQuery(id+"F44.wireOp",EDGE,"E22.right")])]})]});
            var sketch = newSketch(context, id + "F46", { "sketchPlane" : qUnion([Q0])});
            skLineSegment(sketch, "E23.bottom", {"start": v(0, 12.7) * mm, "end": v(6.35, 12.7) * mm});
            skLineSegment(sketch, "E23.top", {"start": v(0, 19.05) * mm, "end": v(6.35, 19.05) * mm});
            skLineSegment(sketch, "E23.left", {"start": v(0, 12.7) * mm, "end": v(0, 19.05) * mm});
            skLineSegment(sketch, "E23.right", {"start": v(6.35, 12.7) * mm, "end": v(6.35, 19.05) * mm});
            skSolve(sketch);
        }
        {
            var Q0;
            Q0=makeQuery(id+"F46.imprint","IMPRINT",FACE,{"disambiguationData":[TD([[makeQuery(id+"F46.imprint","IMPRINT",EDGE,{"derivedFrom":sQuery(id+"F46.wireOp",EDGE,"E23.bottom")}),1.0]])]});
            extrude(context, id + "F47", {"entities" : qUnion([Q0]), "operationType" : NewBodyOperationType.ADD, "oppositeDirection" : true, "depth" : 19.05 * mm});
        }
        {
            var Q0;
            Q0=makeQuery(id+"F47.boolean.opBoolean","MERGE",FACE,{"derivedFrom":[makeQuery(id+"F45.opExtrude","CAP_FACE",FACE,{"disambiguationData":[OSD([sQuery(id+"F44.wireOp",EDGE,"E22.bottom"),sQuery(id+"F44.wireOp",EDGE,"E22.top"),sQuery(id+"F44.wireOp",EDGE,"E22.left"),sQuery(id+"F44.wireOp",EDGE,"E22.right")])],"isStart":false}),makeQuery(id+"F47.opExtrude","SWEPT_FACE",FACE,{"disambiguationData":[OSD([sQuery(id+"F46.wireOp",EDGE,"E23.left")])]})]});
            var sketch = newSketch(context, id + "F48", { "sketchPlane" : qUnion([Q0])});
            skLineSegment(sketch, "E24.bottom", {"start": v(-44.45, 12.7) * mm, "end": v(-38.1, 12.7) * mm});
            skLineSegment(sketch, "E24.top", {"start": v(-44.45, 19.05) * mm, "end": v(-38.1, 19.05) * mm});
            skLineSegment(sketch, "E24.left", {"start": v(-44.45, 12.7) * mm, "end": v(-44.45, 19.05) * mm});
            skLineSegment(sketch, "E24.right", {"start": v(-38.1, 12.7) * mm, "end": v(-38.1, 19.05) * mm});
            skSolve(sketch);
        }
        {
            var Q0;
            Q0=makeQuery(id+"F48.imprint","IMPRINT",FACE,{"disambiguationData":[TD([[makeQuery(id+"F48.imprint","IMPRINT",EDGE,{"derivedFrom":sQuery(id+"F48.wireOp",EDGE,"E24.bottom")}),-1.0]])]});
            extrude(context, id + "F49", {"entities" : qUnion([Q0]), "operationType" : NewBodyOperationType.ADD, "oppositeDirection" : true, "depth" : 19.05 * mm});
        }
        {
            var Q0;
            Q0=makeQuery(id+"F49.boolean.opBoolean","MERGE",FACE,{"derivedFrom":[makeQuery(id+"F47.boolean.opBoolean","MERGE",FACE,{"derivedFrom":[makeQuery(id+"F45.opExtrude","SWEPT_FACE",FACE,{"disambiguationData":[OSD([sQuery(id+"F44.wireOp",EDGE,"E22.top")])]}),makeQuery(id+"F47.opExtrude","SWEPT_FACE",FACE,{"disambiguationData":[OSD([sQuery(id+"F46.wireOp",EDGE,"E23.top")])]})]}),makeQuery(id+"F49.opExtrude","SWEPT_FACE",FACE,{"disambiguationData":[OSD([sQuery(id+"F48.wireOp",EDGE,"E24.top")])]})]});
            var sketch = newSketch(context, id + "F50", { "sketchPlane" : qUnion([Q0])});
            skLineSegment(sketch, "E25.bottom", {"start": v(44.45, -19.05) * mm, "end": v(38.1, -19.05) * mm});
            skLineSegment(sketch, "E25.top", {"start": v(44.45, -12.7) * mm, "end": v(38.1, -12.7) * mm});
            skLineSegment(sketch, "E25.left", {"start": v(44.45, -19.05) * mm, "end": v(44.45, -12.7) * mm});
            skLineSegment(sketch, "E25.right", {"start": v(38.1, -19.05) * mm, "end": v(38.1, -12.7) * mm});
            skSolve(sketch);
        }
        {
            var Q0;
            Q0=makeQuery(id+"F50.imprint","IMPRINT",FACE,{"disambiguationData":[TD([[makeQuery(id+"F50.imprint","IMPRINT",EDGE,{"derivedFrom":sQuery(id+"F50.wireOp",EDGE,"E25.bottom")}),-1.0]])]});
            extrude(context, id + "F51", {"entities" : qUnion([Q0]), "operationType" : NewBodyOperationType.ADD, "oppositeDirection" : true, "depth" : 19.05 * mm});
        }
        {
            var Q0;
            Q0=makeQuery(id+"F51.boolean.opBoolean","MERGE",FACE,{"derivedFrom":[makeQuery(id+"F49.opExtrude","CAP_FACE",FACE,{"disambiguationData":[OSD([sQuery(id+"F48.wireOp",EDGE,"E24.bottom"),sQuery(id+"F48.wireOp",EDGE,"E24.top"),sQuery(id+"F48.wireOp",EDGE,"E24.left"),sQuery(id+"F48.wireOp",EDGE,"E24.right")])],"isStart":false}),makeQuery(id+"F51.opExtrude","SWEPT_FACE",FACE,{"disambiguationData":[OSD([sQuery(id+"F50.wireOp",EDGE,"E25.bottom")])]})]});
            var sketch = newSketch(context, id + "F52", { "sketchPlane" : qUnion([Q0])});
            skLineSegment(sketch, "E26.bottom", {"start": v(44.45, 0) * mm, "end": v(38.1, 0) * mm});
            skLineSegment(sketch, "E26.top", {"start": v(44.45, 6.35) * mm, "end": v(38.1, 6.35) * mm});
            skLineSegment(sketch, "E26.left", {"start": v(44.45, 0) * mm, "end": v(44.45, 6.35) * mm});
            skLineSegment(sketch, "E26.right", {"start": v(38.1, 0) * mm, "end": v(38.1, 6.35) * mm});
            skSolve(sketch);
        }
        {
            var Q0;
            Q0=makeQuery(id+"F52.imprint","IMPRINT",FACE,{"disambiguationData":[TD([[makeQuery(id+"F52.imprint","IMPRINT",EDGE,{"derivedFrom":sQuery(id+"F52.wireOp",EDGE,"E26.bottom")}),-1.0]])]});
            extrude(context, id + "F53", {"entities" : qUnion([Q0]), "operationType" : NewBodyOperationType.ADD, "oppositeDirection" : true, "depth" : 19.05 * mm});
        }
        {
            var Q0;
            Q0=makeQuery(id+"F53.boolean.opBoolean","MERGE",FACE,{"derivedFrom":[makeQuery(id+"F51.boolean.opBoolean","MERGE",FACE,{"derivedFrom":[makeQuery(id+"F49.boolean.opBoolean","MERGE",FACE,{"derivedFrom":[makeQuery(id+"F47.opExtrude","CAP_FACE",FACE,{"disambiguationData":[OSD([sQuery(id+"F46.wireOp",EDGE,"E23.bottom"),sQuery(id+"F46.wireOp",EDGE,"E23.top"),sQuery(id+"F46.wireOp",EDGE,"E23.left"),sQuery(id+"F46.wireOp",EDGE,"E23.right")])],"isStart":false}),makeQuery(id+"F49.opExtrude","SWEPT_FACE",FACE,{"disambiguationData":[OSD([sQuery(id+"F48.wireOp",EDGE,"E24.left")])]})]}),makeQuery(id+"F51.opExtrude","SWEPT_FACE",FACE,{"disambiguationData":[OSD([sQuery(id+"F50.wireOp",EDGE,"E25.left")])]})]}),makeQuery(id+"F53.opExtrude","SWEPT_FACE",FACE,{"disambiguationData":[OSD([sQuery(id+"F52.wireOp",EDGE,"E26.left")])]})]});
            var sketch = newSketch(context, id + "F54", { "sketchPlane" : qUnion([Q0])});
            skLineSegment(sketch, "E27.bottom", {"start": v(0, 0) * mm, "end": v(-6.35, 0) * mm});
            skLineSegment(sketch, "E27.top", {"start": v(0, 6.35) * mm, "end": v(-6.35, 6.35) * mm});
            skLineSegment(sketch, "E27.left", {"start": v(0, 0) * mm, "end": v(0, 6.35) * mm});
            skLineSegment(sketch, "E27.right", {"start": v(-6.35, 0) * mm, "end": v(-6.35, 6.35) * mm});
            skSolve(sketch);
        }
        {
            var Q0;
            Q0=makeQuery(id+"F54.imprint","IMPRINT",FACE,{"disambiguationData":[TD([[makeQuery(id+"F54.imprint","IMPRINT",EDGE,{"derivedFrom":sQuery(id+"F54.wireOp",EDGE,"E27.bottom")}),-1.0]])]});
            extrude(context, id + "F55", {"entities" : qUnion([Q0]), "operationType" : NewBodyOperationType.ADD, "oppositeDirection" : true, "depth" : 19.05 * mm});
        }
        {
            var Q0;
            Q0=makeQuery(id+"F55.boolean.opBoolean","MERGE",FACE,{"derivedFrom":[makeQuery(id+"F53.opExtrude","CAP_FACE",FACE,{"disambiguationData":[OSD([sQuery(id+"F52.wireOp",EDGE,"E26.bottom"),sQuery(id+"F52.wireOp",EDGE,"E26.top"),sQuery(id+"F52.wireOp",EDGE,"E26.left"),sQuery(id+"F52.wireOp",EDGE,"E26.right")])],"isStart":false}),makeQuery(id+"F55.opExtrude","SWEPT_FACE",FACE,{"disambiguationData":[OSD([sQuery(id+"F54.wireOp",EDGE,"E27.left")])]})]});
            var sketch = newSketch(context, id + "F56", { "sketchPlane" : qUnion([Q0])});
            skLineSegment(sketch, "E28.bottom", {"start": v(-25.4, 0) * mm, "end": v(-31.75, 0) * mm});
            skLineSegment(sketch, "E28.top", {"start": v(-25.4, 6.35) * mm, "end": v(-31.75, 6.35) * mm});
            skLineSegment(sketch, "E28.left", {"start": v(-25.4, 0) * mm, "end": v(-25.4, 6.35) * mm});
            skLineSegment(sketch, "E28.right", {"start": v(-31.75, 0) * mm, "end": v(-31.75, 6.35) * mm});
            skSolve(sketch);
        }
        {
            var Q0;
            Q0=makeQuery(id+"F56.imprint","IMPRINT",FACE,{"disambiguationData":[TD([[makeQuery(id+"F56.imprint","IMPRINT",EDGE,{"derivedFrom":sQuery(id+"F56.wireOp",EDGE,"E28.bottom")}),1.0]])]});
            extrude(context, id + "F57", {"entities" : qUnion([Q0]), "operationType" : NewBodyOperationType.ADD, "oppositeDirection" : true, "depth" : 20.95 * mm});
        }
        {
            var Q0;
            Q0=makeQuery(id+"F1.opExtrude","SWEPT_BODY",BODY,{"disambiguationData":[OSD([sQuery(id+"F0.wireOp",EDGE,"E0.bottom"),sQuery(id+"F0.wireOp",EDGE,"E0.top"),sQuery(id+"F0.wireOp",EDGE,"E0.left"),sQuery(id+"F0.wireOp",EDGE,"E0.right")])]});
            var Q1;
            Q1=makeQuery(id+"F57.opExtrude","CAP_FACE",FACE,{"disambiguationData":[OSD([sQuery(id+"F56.wireOp",EDGE,"E28.bottom"),sQuery(id+"F56.wireOp",EDGE,"E28.top"),sQuery(id+"F56.wireOp",EDGE,"E28.left"),sQuery(id+"F56.wireOp",EDGE,"E28.right")])],"isStart":false});
            mirror(context, id + "F58", {"operationType" : NewBodyOperationType.ADD, "entities" : qUnion([Q0]), "mirrorPlane" : qUnion([Q1])});
        }
    });
